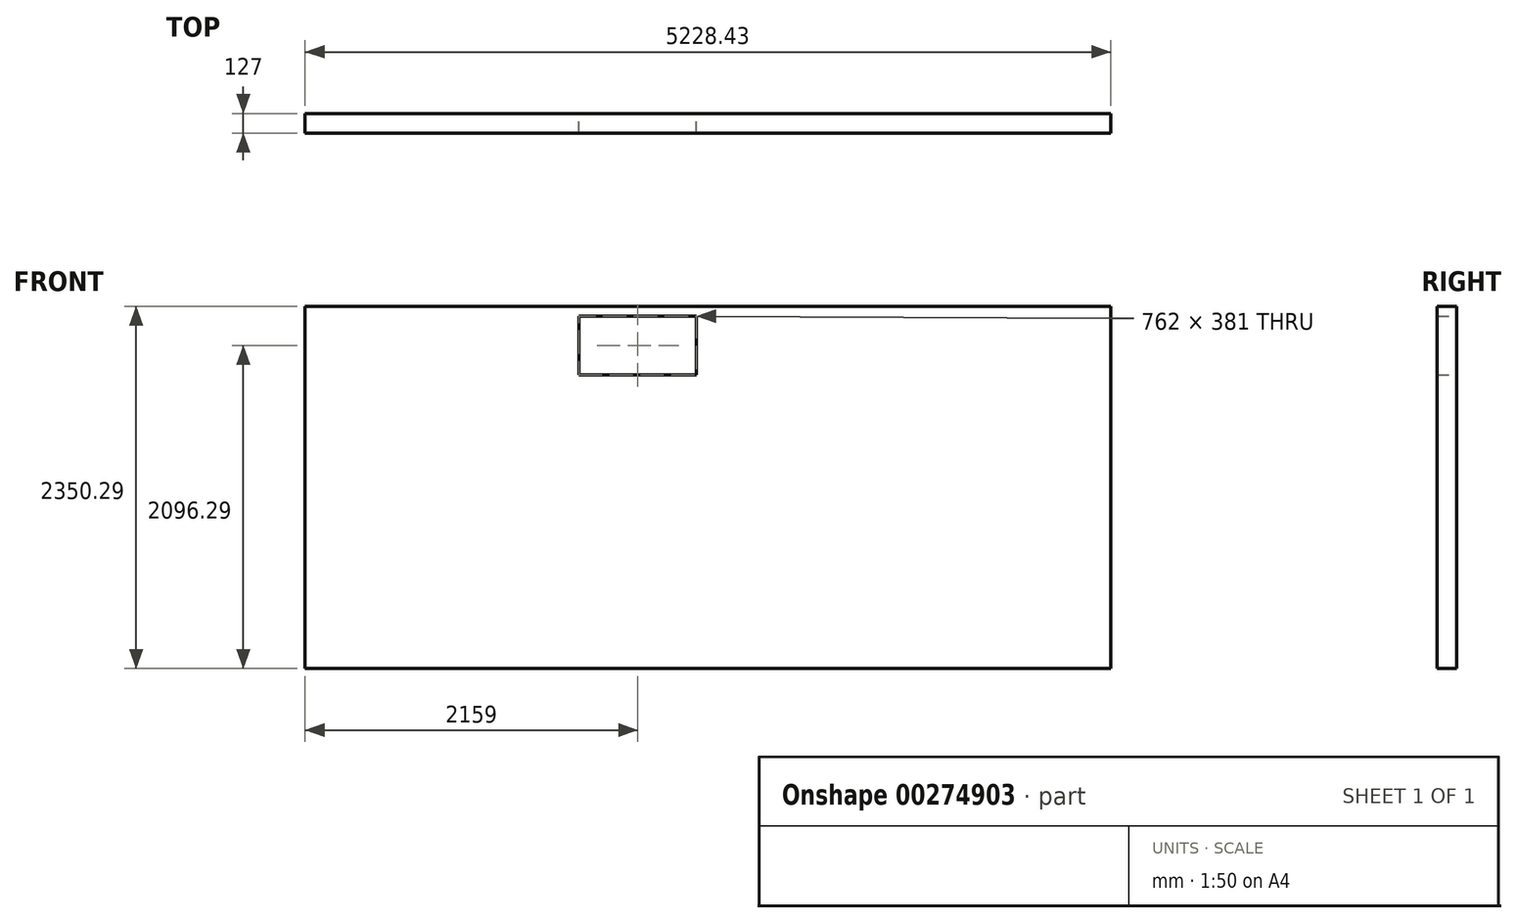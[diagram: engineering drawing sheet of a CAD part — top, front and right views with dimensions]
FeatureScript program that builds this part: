
annotation { "Feature Type Name" : "Feature", "Feature Type Description" : "" }
export const myFeature = defineFeature(function(context is Context, id is Id, definition is map)
    precondition{}
    {
        {
            var Q0;
            Q0=qCreatedBy(makeId("Top.planeOp"),FACE);
            var sketch = newSketch(context, id + "F0", { "sketchPlane" : qUnion([Q0])});
            skLineSegment(sketch, "E0.bottom", {"start": v(0, 0) * mm, "end": v(18288, 0) * mm});
            skLineSegment(sketch, "E0.top", {"start": v(0, 5486.4) * mm, "end": v(18288, 5486.4) * mm});
            skLineSegment(sketch, "E0.left", {"start": v(0, 0) * mm, "end": v(0, 5486.4) * mm});
            skLineSegment(sketch, "E0.right", {"start": v(18288, 0) * mm, "end": v(18288, 5486.4) * mm});
            skSolve(sketch);
        }
        {
            var Q0;
            Q0=makeQuery(id+"F0.imprint","IMPRINT",FACE,{"disambiguationData":[TD([[makeQuery(id+"F0.imprint","IMPRINT",EDGE,{"derivedFrom":sQuery(id+"F0.wireOp",EDGE,"E0.bottom")}),1.0]])]});
            extrude(context, id + "F1", {"entities" : qUnion([Q0]), "depth" : 101.6 * mm});
        }
        {
            var Q0;
            Q0=makeQuery(id+"F1.opExtrude","CAP_FACE",FACE,{"disambiguationData":[OSD([sQuery(id+"F0.wireOp",EDGE,"E0.bottom"),sQuery(id+"F0.wireOp",EDGE,"E0.top"),sQuery(id+"F0.wireOp",EDGE,"E0.left"),sQuery(id+"F0.wireOp",EDGE,"E0.right")])],"isStart":false});
            var sketch = newSketch(context, id + "F2", { "sketchPlane" : qUnion([Q0])});
            skLineSegment(sketch, "E1.bottom", {"start": v(18288, 5486.4) * mm, "end": v(13335, 5486.4) * mm, "construction": true});
            skLineSegment(sketch, "E1.top", {"start": v(18288, 2128.84) * mm, "end": v(13335, 2128.84) * mm, "construction": true});
            skLineSegment(sketch, "E1.left", {"start": v(18288, 5486.4) * mm, "end": v(18288, 2128.84) * mm, "construction": true});
            skLineSegment(sketch, "E1.right", {"start": v(13335, 5486.4) * mm, "end": v(13335, 2128.84) * mm, "construction": true});
            skLineSegment(sketch, "E2.bottom", {"start": v(18288, 2128.84) * mm, "end": v(13335, 2128.84) * mm});
            skLineSegment(sketch, "E2.top", {"start": v(18288, 1976.44) * mm, "end": v(13335, 1976.44) * mm});
            skLineSegment(sketch, "E2.left", {"start": v(18288, 2128.84) * mm, "end": v(18288, 1976.44) * mm});
            skLineSegment(sketch, "E2.right", {"start": v(13335, 2128.84) * mm, "end": v(13335, 1976.44) * mm});
            skLineSegment(sketch, "E3.bottom", {"start": v(13335, 5486.4) * mm, "end": v(13182.6, 5486.4) * mm});
            skLineSegment(sketch, "E3.top", {"start": v(13335, 2128.84) * mm, "end": v(13182.6, 2128.84) * mm});
            skLineSegment(sketch, "E3.left", {"start": v(13335, 5486.4) * mm, "end": v(13335, 2128.84) * mm});
            skLineSegment(sketch, "E3.right", {"start": v(13182.6, 5486.4) * mm, "end": v(13182.6, 2128.84) * mm});
            skLineSegment(sketch, "E4.bottom", {"start": v(13335, 1976.44) * mm, "end": v(13182.6, 1976.44) * mm});
            skLineSegment(sketch, "E4.left", {"start": v(13335, 1976.44) * mm, "end": v(13335, 2128.84) * mm});
            skLineSegment(sketch, "E4.right", {"start": v(13182.6, 1976.44) * mm, "end": v(13182.6, 2128.84) * mm});
            skSolve(sketch);
        }
        {
            var Q0;
            Q0=makeQuery(id+"F2.imprint","IMPRINT",FACE,{"disambiguationData":[TD([[makeQuery(id+"F2.imprint","IMPRINT",EDGE,{"derivedFrom":sQuery(id+"F2.wireOp",EDGE,"E2.bottom")}),1.0]])]});
            var Q1;
            Q1=makeQuery(id+"F2.imprint","IMPRINT",FACE,{"disambiguationData":[TD([[makeQuery(id+"F2.imprint","IMPRINT",EDGE,{"derivedFrom":sQuery(id+"F2.wireOp",EDGE,"E3.bottom")}),-1.0]])]});
            var Q2;
            Q2=makeQuery(id+"F2.imprint","IMPRINT",FACE,{"disambiguationData":[TD([[makeQuery(id+"F2.imprint","IMPRINT",EDGE,{"derivedFrom":sQuery(id+"F2.wireOp",EDGE,"E4.bottom")}),-1.0]])]});
            extrude(context, id + "F3", {"entities" : qUnion([Q0, Q1, Q2]), "operationType" : NewBodyOperationType.ADD, "depth" : 2426.5 * mm});
        }
        {
            var Q0;
            Q0=makeQuery(id+"F3.boolean.opBoolean","MERGE",FACE,{"derivedFrom":[makeQuery(id+"F1.opExtrude","SWEPT_FACE",FACE,{"disambiguationData":[OSD([sQuery(id+"F0.wireOp",EDGE,"E0.right")])]}),makeQuery(id+"F3.opExtrude","SWEPT_FACE",FACE,{"disambiguationData":[OSD([sQuery(id+"F2.wireOp",EDGE,"E2.left")])]})]});
            extrude(context, id + "F4", {"entities" : qUnion([Q0]), "operationType" : NewBodyOperationType.ADD, "depth" : 152.4 * mm});
        }
        {
            var Q0;
            {var subQ0=sQuery(id+"F0.wireOp",EDGE,"E0.top");Q0=makeQuery(id+"F4.boolean.opBoolean","MERGE",FACE,{"derivedFrom":[makeQuery(id+"F3.boolean.opBoolean","MERGE",FACE,{"derivedFrom":[makeQuery(id+"F1.opExtrude","SWEPT_FACE",FACE,{"disambiguationData":[OSD([subQ0])]}),makeQuery(id+"F3.opExtrude","SWEPT_FACE",FACE,{"disambiguationData":[OSD([sQuery(id+"F2.wireOp",EDGE,"E3.bottom")])]})]}),makeQuery(id+"F4.opExtrude","SWEPT_FACE",FACE,{"disambiguationData":[OSD([subQ0,sQuery(id+"F0.wireOp",EDGE,"E0.right")])]})]});}
            extrude(context, id + "F5", {"entities" : qUnion([Q0]), "operationType" : NewBodyOperationType.ADD, "depth" : 152.4 * mm});
        }
        {
            var Q0;
            {var subQ0=sQuery(id+"F0.wireOp",EDGE,"E0.right");var subQ1=sQuery(id+"F0.wireOp",EDGE,"E0.top");var subQ3=makeQuery(id+"F1.opExtrude","SWEPT_FACE",FACE,{"disambiguationData":[OSD([subQ0])]});var subQ4=makeQuery(id+"F1.opExtrude","SWEPT_FACE",FACE,{"disambiguationData":[OSD([subQ1])]});var subQ5=makeQuery(id+"F1.opExtrude","CAP_FACE",FACE,{"disambiguationData":[OSD([sQuery(id+"F0.wireOp",EDGE,"E0.bottom"),subQ1,sQuery(id+"F0.wireOp",EDGE,"E0.left"),subQ0])],"isStart":false});var subQ8=makeQuery(id+"F3.opExtrude","SWEPT_FACE",FACE,{"disambiguationData":[OSD([sQuery(id+"F2.wireOp",EDGE,"E2.bottom")])]});Q0=makeQuery(id+"F5.boolean.opBoolean","MERGE",FACE,{"derivedFrom":[makeQuery(id+"F4.boolean.opBoolean","MERGE",FACE,{"derivedFrom":[makeQuery(id+"F3.boolean.opBoolean","SPLIT",FACE,{"disambiguationData":[TD([subQ8])],"derivedFrom":subQ5}),makeQuery(id+"F4.opExtrude","SWEPT_FACE",FACE,{"disambiguationData":[OSD([subQ0]),TDD([makeQuery(id+"F3.boolean.opBoolean","SPLIT",EDGE,{"disambiguationData":[TD([subQ4])],"derivedFrom":makeQuery(id+"F1.opExtrude","CAP_EDGE",EDGE,{"disambiguationData":[OSD([subQ0])],"isStart":false})})])]})]}),makeQuery(id+"F5.opExtrude","SWEPT_FACE",FACE,{"disambiguationData":[OSD([subQ1,subQ0]),TDD([makeQuery(id+"F4.boolean.opBoolean","MERGE",EDGE,{"derivedFrom":[makeQuery(id+"F3.boolean.opBoolean","SPLIT",EDGE,{"disambiguationData":[TD([subQ3])],"derivedFrom":makeQuery(id+"F1.opExtrude","CAP_EDGE",EDGE,{"disambiguationData":[OSD([subQ1])],"isStart":false})}),makeQuery(id+"F4.opExtrude","SWEPT_EDGE",EDGE,{"disambiguationData":[OSD([subQ1,subQ0]),TDD([makeQuery(id+"F1.opExtrude","CAP_VERTEX",VERTEX,{"disambiguationData":[OSD([subQ1,subQ0])],"isStart":false})])]})]})])]})]});}
            var sketch = newSketch(context, id + "F6", { "sketchPlane" : qUnion([Q0])});
            skLineSegment(sketch, "E5.bottom", {"start": v(18440.4, 2128.84) * mm, "end": v(18288, 2128.84) * mm});
            skLineSegment(sketch, "E5.top", {"start": v(18440.4, 5638.8) * mm, "end": v(18288, 5638.8) * mm});
            skLineSegment(sketch, "E5.left", {"start": v(18440.4, 2128.84) * mm, "end": v(18440.4, 5638.8) * mm});
            skLineSegment(sketch, "E5.right", {"start": v(18288, 2128.84) * mm, "end": v(18288, 5638.8) * mm});
            skLineSegment(sketch, "E6.bottom", {"start": v(13335, 5638.8) * mm, "end": v(18288, 5638.8) * mm});
            skLineSegment(sketch, "E6.top", {"start": v(13335, 5486.4) * mm, "end": v(18288, 5486.4) * mm});
            skLineSegment(sketch, "E6.left", {"start": v(13335, 5638.8) * mm, "end": v(13335, 5486.4) * mm});
            skLineSegment(sketch, "E6.right", {"start": v(18288, 5638.8) * mm, "end": v(18288, 5486.4) * mm});
            skSolve(sketch);
        }
        {
            var Q0;
            Q0=makeQuery(id+"F6.imprint","IMPRINT",FACE,{"disambiguationData":[TD([[makeQuery(id+"F6.imprint","IMPRINT",EDGE,{"derivedFrom":sQuery(id+"F6.wireOp",EDGE,"E6.bottom")}),-1.0]])]});
            var Q1;
            Q1=makeQuery(id+"F6.imprint","IMPRINT",FACE,{"disambiguationData":[TD([[makeQuery(id+"F6.imprint","IMPRINT",EDGE,{"derivedFrom":sQuery(id+"F6.wireOp",EDGE,"E5.bottom")}),-1.0]])]});
            extrude(context, id + "F7", {"entities" : qUnion([Q0, Q1]), "operationType" : NewBodyOperationType.ADD, "depth" : 2350.3 * mm});
        }
        {
            var Q0;
            {var subQ0=sQuery(id+"F2.wireOp",EDGE,"E3.bottom");var subQ1=sQuery(id+"F2.wireOp",EDGE,"E2.left");Q0=makeQuery(id+"F5.boolean.opBoolean","MERGE",FACE,{"derivedFrom":[makeQuery(id+"F4.boolean.opBoolean","MERGE",FACE,{"derivedFrom":[makeQuery(id+"F3.opExtrude","CAP_FACE",FACE,{"disambiguationData":[OSD([sQuery(id+"F2.wireOp",EDGE,"E2.bottom"),sQuery(id+"F2.wireOp",EDGE,"E2.top"),subQ1,subQ0,sQuery(id+"F2.wireOp",EDGE,"E3.left"),sQuery(id+"F2.wireOp",EDGE,"E3.right"),sQuery(id+"F2.wireOp",EDGE,"E4.bottom"),sQuery(id+"F2.wireOp",EDGE,"E4.right")])],"isStart":false}),makeQuery(id+"F4.opExtrude","SWEPT_FACE",FACE,{"disambiguationData":[OSD([subQ1])]})]}),makeQuery(id+"F5.opExtrude","SWEPT_FACE",FACE,{"disambiguationData":[OSD([subQ0])]})]});}
            extrude(context, id + "F8", {"entities" : qUnion([Q0]), "operationType" : NewBodyOperationType.REMOVE, "oppositeDirection" : true, "depth" : 76.2 * mm});
        }
        {
            var Q0;
            {var subQ0=sQuery(id+"F0.wireOp",EDGE,"E0.right");var subQ1=sQuery(id+"F0.wireOp",EDGE,"E0.top");var subQ3=makeQuery(id+"F1.opExtrude","SWEPT_FACE",FACE,{"disambiguationData":[OSD([subQ0])]});var subQ4=makeQuery(id+"F1.opExtrude","SWEPT_FACE",FACE,{"disambiguationData":[OSD([subQ1])]});var subQ5=makeQuery(id+"F1.opExtrude","CAP_FACE",FACE,{"disambiguationData":[OSD([sQuery(id+"F0.wireOp",EDGE,"E0.bottom"),subQ1,sQuery(id+"F0.wireOp",EDGE,"E0.left"),subQ0])],"isStart":false});var subQ8=makeQuery(id+"F3.opExtrude","SWEPT_FACE",FACE,{"disambiguationData":[OSD([sQuery(id+"F2.wireOp",EDGE,"E2.bottom")])]});Q0=makeQuery(id+"F5.boolean.opBoolean","MERGE",FACE,{"derivedFrom":[makeQuery(id+"F4.boolean.opBoolean","MERGE",FACE,{"derivedFrom":[makeQuery(id+"F3.boolean.opBoolean","SPLIT",FACE,{"disambiguationData":[TD([subQ8])],"derivedFrom":subQ5}),makeQuery(id+"F4.opExtrude","SWEPT_FACE",FACE,{"disambiguationData":[OSD([subQ0]),TDD([makeQuery(id+"F3.boolean.opBoolean","SPLIT",EDGE,{"disambiguationData":[TD([subQ4])],"derivedFrom":makeQuery(id+"F1.opExtrude","CAP_EDGE",EDGE,{"disambiguationData":[OSD([subQ0])],"isStart":false})})])]})]}),makeQuery(id+"F5.opExtrude","SWEPT_FACE",FACE,{"disambiguationData":[OSD([subQ1,subQ0]),TDD([makeQuery(id+"F4.boolean.opBoolean","MERGE",EDGE,{"derivedFrom":[makeQuery(id+"F3.boolean.opBoolean","SPLIT",EDGE,{"disambiguationData":[TD([subQ3])],"derivedFrom":makeQuery(id+"F1.opExtrude","CAP_EDGE",EDGE,{"disambiguationData":[OSD([subQ1])],"isStart":false})}),makeQuery(id+"F4.opExtrude","SWEPT_EDGE",EDGE,{"disambiguationData":[OSD([subQ1,subQ0]),TDD([makeQuery(id+"F1.opExtrude","CAP_VERTEX",VERTEX,{"disambiguationData":[OSD([subQ1,subQ0])],"isStart":false})])]})]})])]})]});}
            var sketch = newSketch(context, id + "F9", { "sketchPlane" : qUnion([Q0])});
            skLineSegment(sketch, "E7.bottom", {"start": v(18288, 5486.4) * mm, "end": v(17907, 5486.4) * mm});
            skLineSegment(sketch, "E7.top", {"start": v(18288, 5207) * mm, "end": v(17907, 5207) * mm});
            skLineSegment(sketch, "E7.left", {"start": v(18288, 5486.4) * mm, "end": v(18288, 5207) * mm});
            skLineSegment(sketch, "E7.right", {"start": v(17907, 5486.4) * mm, "end": v(17907, 5207) * mm});
            skSolve(sketch);
        }
        {
            var Q0;
            Q0=makeQuery(id+"F9.imprint","IMPRINT",FACE,{"disambiguationData":[TD([[makeQuery(id+"F9.imprint","IMPRINT",EDGE,{"derivedFrom":sQuery(id+"F9.wireOp",EDGE,"E7.bottom")}),-1.0]])]});
            var Q1;
            Q1=makeQuery(id+"F8.boolean.opBoolean","MERGE",FACE,{"derivedFrom":[makeQuery(id+"F7.opExtrude","CAP_FACE",FACE,{"disambiguationData":[OSD([sQuery(id+"F6.wireOp",EDGE,"E5.bottom"),sQuery(id+"F6.wireOp",EDGE,"E5.top"),sQuery(id+"F6.wireOp",EDGE,"E5.left"),sQuery(id+"F6.wireOp",EDGE,"E5.right"),sQuery(id+"F6.wireOp",EDGE,"E6.bottom"),sQuery(id+"F6.wireOp",EDGE,"E6.top"),sQuery(id+"F6.wireOp",EDGE,"E6.left")])],"isStart":false}),makeQuery(id+"F8.opExtrude","CAP_FACE",FACE,{"disambiguationData":[OSD([sQuery(id+"F2.wireOp",EDGE,"E2.bottom"),sQuery(id+"F2.wireOp",EDGE,"E2.top"),sQuery(id+"F2.wireOp",EDGE,"E2.left"),sQuery(id+"F2.wireOp",EDGE,"E3.bottom"),sQuery(id+"F2.wireOp",EDGE,"E3.left"),sQuery(id+"F2.wireOp",EDGE,"E3.right"),sQuery(id+"F2.wireOp",EDGE,"E4.bottom"),sQuery(id+"F2.wireOp",EDGE,"E4.right")])],"isStart":false})]});
            extrude(context, id + "F10", {"entities" : qUnion([Q0]), "operationType" : NewBodyOperationType.ADD, "endBound" : BoundingType.UP_TO_SURFACE, "endBoundEntityFace" : qUnion([Q1]), "depth" : 25.4 * mm});
        }
        {
            var Q0;
            Q0=makeQuery(id+"F10.opExtrude","SWEPT_FACE",FACE,{"disambiguationData":[OSD([sQuery(id+"F9.wireOp",EDGE,"E7.top")])]});
            extrude(context, id + "F11", {"entities" : qUnion([Q0]), "operationType" : NewBodyOperationType.ADD, "depth" : 101.6 * mm});
        }
        {
            var Q0;
            {var subQ0=sQuery(id+"F9.wireOp",EDGE,"E7.right");Q0=makeQuery(id+"F11.boolean.opBoolean","MERGE",FACE,{"derivedFrom":[makeQuery(id+"F10.opExtrude","SWEPT_FACE",FACE,{"disambiguationData":[OSD([subQ0])]}),makeQuery(id+"F11.opExtrude","SWEPT_FACE",FACE,{"disambiguationData":[OSD([sQuery(id+"F9.wireOp",EDGE,"E7.top"),subQ0])]})]});}
            extrude(context, id + "F12", {"entities" : qUnion([Q0]), "operationType" : NewBodyOperationType.REMOVE, "oppositeDirection" : true, "depth" : 101.6 * mm});
        }
        {
            var Q0;
            {var subQ0=sQuery(id+"F2.wireOp",EDGE,"E3.right");Q0=makeQuery(id+"F5.boolean.opBoolean","MERGE",FACE,{"derivedFrom":[makeQuery(id+"F3.opExtrude","SWEPT_FACE",FACE,{"disambiguationData":[OSD([subQ0,sQuery(id+"F2.wireOp",EDGE,"E4.right")])]}),makeQuery(id+"F5.opExtrude","SWEPT_FACE",FACE,{"disambiguationData":[OSD([sQuery(id+"F0.wireOp",EDGE,"E0.top"),sQuery(id+"F2.wireOp",EDGE,"E3.bottom"),subQ0])]})]});}
            extrude(context, id + "F13", {"entities" : qUnion([Q0]), "operationType" : NewBodyOperationType.ADD, "depth" : 275.43 * mm});
        }
        {
            var Q0;
            {var subQ0=sQuery(id+"F2.wireOp",EDGE,"E3.left");Q0=makeQuery(id+"F5.boolean.opBoolean","MERGE",FACE,{"derivedFrom":[makeQuery(id+"F3.opExtrude","SWEPT_FACE",FACE,{"disambiguationData":[OSD([subQ0])]}),makeQuery(id+"F5.opExtrude","SWEPT_FACE",FACE,{"disambiguationData":[OSD([sQuery(id+"F0.wireOp",EDGE,"E0.top"),sQuery(id+"F2.wireOp",EDGE,"E3.bottom"),subQ0])]})]});}
            extrude(context, id + "F14", {"entities" : qUnion([Q0]), "operationType" : NewBodyOperationType.REMOVE, "oppositeDirection" : true, "depth" : 275.43 * mm});
        }
        {
            var Q0;
            {var subQ0=sQuery(id+"F2.wireOp",EDGE,"E4.bottom");var subQ1=sQuery(id+"F2.wireOp",EDGE,"E2.top");Q0=makeQuery(id+"F13.boolean.opBoolean","MERGE",FACE,{"derivedFrom":[makeQuery(id+"F4.boolean.opBoolean","MERGE",FACE,{"derivedFrom":[makeQuery(id+"F3.opExtrude","SWEPT_FACE",FACE,{"disambiguationData":[OSD([subQ1,subQ0])]}),makeQuery(id+"F4.opExtrude","SWEPT_FACE",FACE,{"disambiguationData":[OSD([sQuery(id+"F0.wireOp",EDGE,"E0.right"),subQ1,sQuery(id+"F2.wireOp",EDGE,"E2.left")])]})]}),makeQuery(id+"F13.opExtrude","SWEPT_FACE",FACE,{"disambiguationData":[OSD([subQ0,sQuery(id+"F2.wireOp",EDGE,"E4.right")])]})]});}
            extrude(context, id + "F15", {"entities" : qUnion([Q0]), "operationType" : NewBodyOperationType.REMOVE, "oppositeDirection" : true, "depth" : 25.4 * mm});
        }
        {
            var Q0;
            {var subQ0=sQuery(id+"F2.wireOp",EDGE,"E2.bottom");Q0=makeQuery(id+"F14.boolean.opBoolean","MERGE",FACE,{"derivedFrom":[makeQuery(id+"F4.boolean.opBoolean","MERGE",FACE,{"derivedFrom":[makeQuery(id+"F3.opExtrude","SWEPT_FACE",FACE,{"disambiguationData":[OSD([subQ0])]}),makeQuery(id+"F4.opExtrude","SWEPT_FACE",FACE,{"disambiguationData":[OSD([sQuery(id+"F0.wireOp",EDGE,"E0.right"),subQ0,sQuery(id+"F2.wireOp",EDGE,"E2.left")])]})]}),makeQuery(id+"F14.opExtrude","SWEPT_FACE",FACE,{"disambiguationData":[OSD([subQ0,sQuery(id+"F2.wireOp",EDGE,"E3.left"),sQuery(id+"F2.wireOp",EDGE,"E3.top"),sQuery(id+"F2.wireOp",EDGE,"E4.left")])]})]});}
            var sketch = newSketch(context, id + "F16", { "sketchPlane" : qUnion([Q0])});
            skLineSegment(sketch, "E8.bottom", {"start": v(-13059.57, 2451.9) * mm, "end": v(-14431.17, 2451.9) * mm, "construction": true});
            skLineSegment(sketch, "E8.top", {"start": v(-13059.57, 2197.9) * mm, "end": v(-14431.17, 2197.9) * mm, "construction": true});
            skLineSegment(sketch, "E8.left", {"start": v(-13059.57, 2451.9) * mm, "end": v(-13059.57, 2197.9) * mm, "construction": true});
            skLineSegment(sketch, "E8.right", {"start": v(-14431.17, 2451.9) * mm, "end": v(-14431.17, 2197.9) * mm, "construction": true});
            skLineSegment(sketch, "E9.bottom", {"start": v(-14431.17, 2197.9) * mm, "end": v(-15193.17, 2197.9) * mm});
            skLineSegment(sketch, "E9.top", {"start": v(-14431.17, 1943.9) * mm, "end": v(-15193.17, 1943.9) * mm});
            skLineSegment(sketch, "E9.left", {"start": v(-14431.17, 2197.9) * mm, "end": v(-14431.17, 1943.9) * mm});
            skLineSegment(sketch, "E9.right", {"start": v(-15193.17, 2197.9) * mm, "end": v(-15193.17, 1943.9) * mm});
            skSolve(sketch);
        }
        {
            var Q0;
            Q0=makeQuery(id+"F16.imprint","IMPRINT",FACE,{"disambiguationData":[TD([[makeQuery(id+"F16.imprint","IMPRINT",EDGE,{"derivedFrom":sQuery(id+"F16.wireOp",EDGE,"E9.bottom")}),1.0]])]});
            extrude(context, id + "F17", {"entities" : qUnion([Q0]), "operationType" : NewBodyOperationType.REMOVE, "endBound" : BoundingType.THROUGH_ALL, "oppositeDirection" : true, "depth" : 25.4 * mm});
        }
        {
            var Q0;
            Q0=makeQuery(id+"F17.boolean.opBoolean","COPY",FACE,{"derivedFrom":makeQuery(id+"F17.opExtrude","SWEPT_FACE",FACE,{"disambiguationData":[OSD([sQuery(id+"F16.wireOp",EDGE,"E9.bottom")])]})});
            extrude(context, id + "F18", {"entities" : qUnion([Q0]), "operationType" : NewBodyOperationType.REMOVE, "oppositeDirection" : true, "depth" : 190.5 * mm});
        }
        {
            var Q0;
            Q0=makeQuery(id+"F17.boolean.opBoolean","COPY",FACE,{"derivedFrom":makeQuery(id+"F17.opExtrude","SWEPT_FACE",FACE,{"disambiguationData":[OSD([sQuery(id+"F16.wireOp",EDGE,"E9.top")])]})});
            extrude(context, id + "F19", {"entities" : qUnion([Q0]), "operationType" : NewBodyOperationType.ADD, "depth" : 63.5 * mm});
        }
        {
            var Q0;
            Q0=makeQuery(id+"F7.opExtrude","SWEPT_FACE",FACE,{"disambiguationData":[OSD([sQuery(id+"F6.wireOp",EDGE,"E5.right")])]});
            var sketch = newSketch(context, id + "F20", { "sketchPlane" : qUnion([Q0])});
            skLineSegment(sketch, "E10.bottom", {"start": v(-5105.4, 2451.9) * mm, "end": v(-4851.4, 2451.9) * mm, "construction": true});
            skLineSegment(sketch, "E10.top", {"start": v(-5105.4, 2375.7) * mm, "end": v(-4851.4, 2375.7) * mm, "construction": true});
            skLineSegment(sketch, "E10.left", {"start": v(-5105.4, 2451.9) * mm, "end": v(-5105.4, 2375.7) * mm, "construction": true});
            skLineSegment(sketch, "E10.right", {"start": v(-4851.4, 2451.9) * mm, "end": v(-4851.4, 2375.7) * mm, "construction": true});
            skLineSegment(sketch, "E11.bottom", {"start": v(-4851.4, 2375.7) * mm, "end": v(-5105.4, 2375.7) * mm});
            skLineSegment(sketch, "E11.top", {"start": v(-4851.4, 2070.9) * mm, "end": v(-5105.4, 2070.9) * mm});
            skLineSegment(sketch, "E11.left", {"start": v(-4851.4, 2375.7) * mm, "end": v(-4851.4, 2070.9) * mm});
            skLineSegment(sketch, "E11.right", {"start": v(-5105.4, 2375.7) * mm, "end": v(-5105.4, 2070.9) * mm});
            skSolve(sketch);
        }
        {
            var Q0;
            Q0=makeQuery(id+"F20.imprint","IMPRINT",FACE,{"disambiguationData":[TD([[makeQuery(id+"F20.imprint","IMPRINT",EDGE,{"derivedFrom":sQuery(id+"F20.wireOp",EDGE,"E11.bottom")}),1.0]])]});
            extrude(context, id + "F21", {"entities" : qUnion([Q0]), "operationType" : NewBodyOperationType.REMOVE, "endBound" : BoundingType.THROUGH_ALL, "oppositeDirection" : true, "depth" : 25.4 * mm});
        }
        {
            var Q0;
            Q0=makeQuery(id+"F7.opExtrude","SWEPT_FACE",FACE,{"disambiguationData":[OSD([sQuery(id+"F6.wireOp",EDGE,"E5.right")])]});
            var sketch = newSketch(context, id + "F22", { "sketchPlane" : qUnion([Q0])});
            skLineSegment(sketch, "E12.bottom", {"start": v(-4851.4, 2375.7) * mm, "end": v(-3606.8, 2375.7) * mm, "construction": true});
            skLineSegment(sketch, "E12.top", {"start": v(-4851.4, 2070.9) * mm, "end": v(-3606.8, 2070.9) * mm, "construction": true});
            skLineSegment(sketch, "E12.left", {"start": v(-4851.4, 2375.7) * mm, "end": v(-4851.4, 2070.9) * mm, "construction": true});
            skLineSegment(sketch, "E12.right", {"start": v(-3606.8, 2375.7) * mm, "end": v(-3606.8, 2070.9) * mm, "construction": true});
            skLineSegment(sketch, "E13.bottom", {"start": v(-3606.8, 2375.7) * mm, "end": v(-3888.54, 2375.7) * mm});
            skLineSegment(sketch, "E13.top", {"start": v(-3606.8, 2070.9) * mm, "end": v(-3888.54, 2070.9) * mm});
            skLineSegment(sketch, "E13.left", {"start": v(-3606.8, 2375.7) * mm, "end": v(-3606.8, 2070.9) * mm});
            skLineSegment(sketch, "E13.right", {"start": v(-3888.54, 2375.7) * mm, "end": v(-3888.54, 2070.9) * mm});
            skSolve(sketch);
        }
        {
            var Q0;
            Q0=makeQuery(id+"F22.imprint","IMPRINT",FACE,{"disambiguationData":[TD([[makeQuery(id+"F22.imprint","IMPRINT",EDGE,{"derivedFrom":sQuery(id+"F22.wireOp",EDGE,"E13.bottom")}),1.0]])]});
            extrude(context, id + "F23", {"entities" : qUnion([Q0]), "operationType" : NewBodyOperationType.REMOVE, "endBound" : BoundingType.THROUGH_ALL, "oppositeDirection" : true, "depth" : 25.4 * mm});
        }
        {
            var Q0;
            Q0=makeQuery(id+"F23.boolean.opBoolean","COPY",FACE,{"derivedFrom":makeQuery(id+"F23.opExtrude","SWEPT_FACE",FACE,{"disambiguationData":[OSD([sQuery(id+"F22.wireOp",EDGE,"E13.right")])]})});
            extrude(context, id + "F24", {"entities" : qUnion([Q0]), "operationType" : NewBodyOperationType.REMOVE, "oppositeDirection" : true, "depth" : 304.8 * mm});
        }
        {
            var Q0;
            Q0=makeQuery(id+"F23.boolean.opBoolean","COPY",FACE,{"derivedFrom":makeQuery(id+"F23.opExtrude","SWEPT_FACE",FACE,{"disambiguationData":[OSD([sQuery(id+"F22.wireOp",EDGE,"E13.left")])]})});
            extrude(context, id + "F25", {"entities" : qUnion([Q0]), "operationType" : NewBodyOperationType.ADD, "depth" : 304.8 * mm});
        }
        {
            var Q0;
            Q0=makeQuery(id+"F24.boolean.opBoolean","COPY",FACE,{"derivedFrom":makeQuery(id+"F24.opExtrude","CAP_FACE",FACE,{"disambiguationData":[OSD([sQuery(id+"F22.wireOp",EDGE,"E13.right")])],"isStart":false})});
            extrude(context, id + "F26", {"entities" : qUnion([Q0]), "operationType" : NewBodyOperationType.ADD, "depth" : 25.4 * mm});
        }
        {
            var Q0;
            Q0=makeQuery(id+"F25.opExtrude","CAP_FACE",FACE,{"disambiguationData":[OSD([sQuery(id+"F22.wireOp",EDGE,"E13.left")])],"isStart":false});
            extrude(context, id + "F27", {"entities" : qUnion([Q0]), "operationType" : NewBodyOperationType.REMOVE, "oppositeDirection" : true, "depth" : 25.4 * mm});
        }
        {
            var Q0;
            Q0=makeQuery(id+"F27.boolean.opBoolean","COPY",FACE,{"derivedFrom":makeQuery(id+"F27.opExtrude","CAP_FACE",FACE,{"disambiguationData":[OSD([sQuery(id+"F22.wireOp",EDGE,"E13.left")])],"isStart":false})});
            extrude(context, id + "F28", {"entities" : qUnion([Q0]), "operationType" : NewBodyOperationType.REMOVE, "oppositeDirection" : true, "depth" : 12.7 * mm});
        }
        {
            var Q0;
            Q0=makeQuery(id+"F26.opExtrude","CAP_FACE",FACE,{"disambiguationData":[OSD([sQuery(id+"F22.wireOp",EDGE,"E13.right")])],"isStart":false});
            extrude(context, id + "F29", {"entities" : qUnion([Q0]), "operationType" : NewBodyOperationType.ADD, "depth" : 12.7 * mm});
        }
        {
            var Q0;
            Q0=makeQuery(id+"F13.opExtrude","CAP_FACE",FACE,{"disambiguationData":[OSD([sQuery(id+"F0.wireOp",EDGE,"E0.top"),sQuery(id+"F2.wireOp",EDGE,"E3.bottom"),sQuery(id+"F2.wireOp",EDGE,"E3.right"),sQuery(id+"F2.wireOp",EDGE,"E4.right")])],"isStart":false});
            var sketch = newSketch(context, id + "F30", { "sketchPlane" : qUnion([Q0])});
            skLineSegment(sketch, "E14.bottom", {"start": v(-2001.84, 2451.9) * mm, "end": v(-2408.24, 2451.9) * mm, "construction": true});
            skLineSegment(sketch, "E14.top", {"start": v(-2001.84, 1527.67) * mm, "end": v(-2408.24, 1527.67) * mm, "construction": true});
            skLineSegment(sketch, "E14.left", {"start": v(-2001.84, 2451.9) * mm, "end": v(-2001.84, 1527.67) * mm, "construction": true});
            skLineSegment(sketch, "E14.right", {"start": v(-2408.24, 2451.9) * mm, "end": v(-2408.24, 1527.67) * mm, "construction": true});
            skLineSegment(sketch, "E15.bottom", {"start": v(-2408.24, 2451.9) * mm, "end": v(-2535.24, 2451.9) * mm});
            skLineSegment(sketch, "E15.top", {"start": v(-2408.24, 101.6) * mm, "end": v(-2535.24, 101.6) * mm});
            skLineSegment(sketch, "E15.left", {"start": v(-2408.24, 2451.9) * mm, "end": v(-2408.24, 101.6) * mm});
            skLineSegment(sketch, "E15.right", {"start": v(-2535.24, 2451.9) * mm, "end": v(-2535.24, 101.6) * mm});
            skSolve(sketch);
        }
        {
            var Q0;
            Q0=makeQuery(id+"F30.imprint","IMPRINT",FACE,{"disambiguationData":[TD([[makeQuery(id+"F30.imprint","IMPRINT",EDGE,{"derivedFrom":sQuery(id+"F30.wireOp",EDGE,"E15.bottom")}),-1.0]])]});
            var Q1;
            {var subQ0=sQuery(id+"F0.wireOp",EDGE,"E0.left");Q1=makeQuery(id+"F5.boolean.opBoolean","MERGE",FACE,{"derivedFrom":[makeQuery(id+"F1.opExtrude","SWEPT_FACE",FACE,{"disambiguationData":[OSD([subQ0])]}),makeQuery(id+"F5.opExtrude","SWEPT_FACE",FACE,{"disambiguationData":[OSD([sQuery(id+"F0.wireOp",EDGE,"E0.top"),subQ0])]})]});}
            extrude(context, id + "F31", {"entities" : qUnion([Q0]), "operationType" : NewBodyOperationType.ADD, "endBound" : BoundingType.UP_TO_SURFACE, "endBoundEntityFace" : qUnion([Q1]), "depth" : 25.4 * mm});
        }
        {
            var Q0;
            Q0=makeQuery(id+"F31.opExtrude","SWEPT_FACE",FACE,{"disambiguationData":[OSD([sQuery(id+"F30.wireOp",EDGE,"E15.left")])]});
            var sketch = newSketch(context, id + "F32", { "sketchPlane" : qUnion([Q0])});
            skLineSegment(sketch, "E16.bottom", {"start": v(12907.17, 101.6) * mm, "end": v(12805.57, 101.6) * mm, "construction": true});
            skLineSegment(sketch, "E16.top", {"start": v(12907.17, 469.78) * mm, "end": v(12805.57, 469.78) * mm, "construction": true});
            skLineSegment(sketch, "E16.left", {"start": v(12907.17, 101.6) * mm, "end": v(12907.17, 469.78) * mm, "construction": true});
            skLineSegment(sketch, "E16.right", {"start": v(12805.57, 101.6) * mm, "end": v(12805.57, 469.78) * mm, "construction": true});
            skLineSegment(sketch, "E17.bottom", {"start": v(12805.57, 101.6) * mm, "end": v(11230.77, 101.6) * mm});
            skLineSegment(sketch, "E17.top", {"start": v(12805.57, 2235.2) * mm, "end": v(11230.77, 2235.2) * mm});
            skLineSegment(sketch, "E17.left", {"start": v(12805.57, 101.6) * mm, "end": v(12805.57, 2235.2) * mm});
            skLineSegment(sketch, "E17.right", {"start": v(11230.77, 101.6) * mm, "end": v(11230.77, 2235.2) * mm});
            skSolve(sketch);
        }
        {
            var Q0;
            Q0=makeQuery(id+"F32.imprint","IMPRINT",FACE,{"disambiguationData":[TD([[makeQuery(id+"F32.imprint","IMPRINT",EDGE,{"derivedFrom":sQuery(id+"F32.wireOp",EDGE,"E17.bottom")}),1.0]])]});
            extrude(context, id + "F33", {"entities" : qUnion([Q0]), "operationType" : NewBodyOperationType.REMOVE, "endBound" : BoundingType.THROUGH_ALL, "oppositeDirection" : true, "depth" : 25.4 * mm});
        }
        {
            var Q0;
            Q0=makeQuery(id+"F33.boolean.opBoolean","COPY",FACE,{"derivedFrom":makeQuery(id+"F33.opExtrude","SWEPT_FACE",FACE,{"disambiguationData":[OSD([sQuery(id+"F32.wireOp",EDGE,"E17.right")])]})});
            extrude(context, id + "F34", {"entities" : qUnion([Q0]), "operationType" : NewBodyOperationType.REMOVE, "oppositeDirection" : true, "depth" : 1320.8 * mm});
        }
        {
            var Q0;
            Q0=makeQuery(id+"F33.boolean.opBoolean","COPY",FACE,{"derivedFrom":makeQuery(id+"F33.opExtrude","SWEPT_FACE",FACE,{"disambiguationData":[OSD([sQuery(id+"F32.wireOp",EDGE,"E17.left")])]})});
            extrude(context, id + "F35", {"entities" : qUnion([Q0]), "operationType" : NewBodyOperationType.ADD, "depth" : 1320.8 * mm});
        }
        {
            var Q0;
            {var subQ0=sQuery(id+"F22.wireOp",EDGE,"E13.left");var subQ1=sQuery(id+"F22.wireOp",EDGE,"E13.top");Q0=makeQuery(id+"F28.boolean.opBoolean","MERGE",FACE,{"derivedFrom":[makeQuery(id+"F27.boolean.opBoolean","MERGE",FACE,{"derivedFrom":[makeQuery(id+"F24.boolean.opBoolean","MERGE",FACE,{"derivedFrom":[makeQuery(id+"F23.boolean.opBoolean","COPY",FACE,{"derivedFrom":makeQuery(id+"F23.opExtrude","SWEPT_FACE",FACE,{"disambiguationData":[OSD([subQ1])]})}),makeQuery(id+"F24.opExtrude","SWEPT_FACE",FACE,{"disambiguationData":[OSD([subQ1,sQuery(id+"F22.wireOp",EDGE,"E13.right")])]})]}),makeQuery(id+"F27.opExtrude","SWEPT_FACE",FACE,{"disambiguationData":[OSD([subQ1,subQ0])]})]}),makeQuery(id+"F28.opExtrude","SWEPT_FACE",FACE,{"disambiguationData":[OSD([subQ1,subQ0])]})]});}
            extrude(context, id + "F36", {"entities" : qUnion([Q0]), "operationType" : NewBodyOperationType.ADD, "depth" : 120.65 * mm});
        }
        {
            var Q0;
            {var subQ0=sQuery(id+"F22.wireOp",EDGE,"E13.left");var subQ1=sQuery(id+"F22.wireOp",EDGE,"E13.bottom");Q0=makeQuery(id+"F28.boolean.opBoolean","MERGE",FACE,{"derivedFrom":[makeQuery(id+"F27.boolean.opBoolean","MERGE",FACE,{"derivedFrom":[makeQuery(id+"F24.boolean.opBoolean","MERGE",FACE,{"derivedFrom":[makeQuery(id+"F23.boolean.opBoolean","COPY",FACE,{"derivedFrom":makeQuery(id+"F23.opExtrude","SWEPT_FACE",FACE,{"disambiguationData":[OSD([subQ1])]})}),makeQuery(id+"F24.opExtrude","SWEPT_FACE",FACE,{"disambiguationData":[OSD([subQ1,sQuery(id+"F22.wireOp",EDGE,"E13.right")])]})]}),makeQuery(id+"F27.opExtrude","SWEPT_FACE",FACE,{"disambiguationData":[OSD([subQ1,subQ0])]})]}),makeQuery(id+"F28.opExtrude","SWEPT_FACE",FACE,{"disambiguationData":[OSD([subQ1,subQ0])]})]});}
            extrude(context, id + "F37", {"entities" : qUnion([Q0]), "operationType" : NewBodyOperationType.REMOVE, "endBound" : BoundingType.THROUGH_ALL, "oppositeDirection" : true, "depth" : 25.4 * mm});
        }
        {
            var Q0;
            Q0=makeQuery(id+"F21.boolean.opBoolean","COPY",FACE,{"derivedFrom":makeQuery(id+"F21.opExtrude","SWEPT_FACE",FACE,{"disambiguationData":[OSD([sQuery(id+"F20.wireOp",EDGE,"E11.top")])]})});
            extrude(context, id + "F38", {"entities" : qUnion([Q0]), "operationType" : NewBodyOperationType.REMOVE, "oppositeDirection" : true, "depth" : 190.5 * mm});
        }
        {
            var Q0;
            Q0=makeQuery(id+"F21.boolean.opBoolean","COPY",FACE,{"derivedFrom":makeQuery(id+"F21.opExtrude","SWEPT_FACE",FACE,{"disambiguationData":[OSD([sQuery(id+"F20.wireOp",EDGE,"E11.bottom")])]})});
            extrude(context, id + "F39", {"entities" : qUnion([Q0]), "operationType" : NewBodyOperationType.ADD, "depth" : 190.5 * mm});
        }
        {
            var Q0;
            Q0=makeQuery(id+"F39.opExtrude","CAP_FACE",FACE,{"disambiguationData":[OSD([sQuery(id+"F20.wireOp",EDGE,"E11.bottom")])],"isStart":false});
            extrude(context, id + "F40", {"entities" : qUnion([Q0]), "operationType" : NewBodyOperationType.REMOVE, "oppositeDirection" : true, "depth" : 76.2 * mm});
        }
        {
            var Q0;
            {var subQ0=sQuery(id+"F16.wireOp",EDGE,"E9.right");Q0=makeQuery(id+"F18.boolean.opBoolean","MERGE",FACE,{"derivedFrom":[makeQuery(id+"F17.boolean.opBoolean","COPY",FACE,{"derivedFrom":makeQuery(id+"F17.opExtrude","SWEPT_FACE",FACE,{"disambiguationData":[OSD([subQ0])]})}),makeQuery(id+"F18.opExtrude","SWEPT_FACE",FACE,{"disambiguationData":[OSD([sQuery(id+"F16.wireOp",EDGE,"E9.bottom"),subQ0])]})]});}
            extrude(context, id + "F41", {"entities" : qUnion([Q0]), "operationType" : NewBodyOperationType.REMOVE, "oppositeDirection" : true, "depth" : 406.4 * mm});
        }
        {
            var Q0;
            {var subQ0=sQuery(id+"F16.wireOp",EDGE,"E9.left");Q0=makeQuery(id+"F18.boolean.opBoolean","MERGE",FACE,{"derivedFrom":[makeQuery(id+"F17.boolean.opBoolean","COPY",FACE,{"derivedFrom":makeQuery(id+"F17.opExtrude","SWEPT_FACE",FACE,{"disambiguationData":[OSD([subQ0])]})}),makeQuery(id+"F18.opExtrude","SWEPT_FACE",FACE,{"disambiguationData":[OSD([sQuery(id+"F16.wireOp",EDGE,"E9.bottom"),subQ0])]})]});}
            extrude(context, id + "F42", {"entities" : qUnion([Q0]), "operationType" : NewBodyOperationType.ADD, "depth" : 406.4 * mm});
        }
        {
            var Q0;
            {var subQ0=sQuery(id+"F22.wireOp",EDGE,"E13.left");Q0=makeQuery(id+"F37.boolean.opBoolean","MERGE",FACE,{"derivedFrom":[makeQuery(id+"F28.boolean.opBoolean","COPY",FACE,{"derivedFrom":makeQuery(id+"F28.opExtrude","CAP_FACE",FACE,{"disambiguationData":[OSD([subQ0])],"isStart":false})}),makeQuery(id+"F37.opExtrude","SWEPT_FACE",FACE,{"disambiguationData":[OSD([sQuery(id+"F22.wireOp",EDGE,"E13.bottom"),subQ0])]})]});}
            extrude(context, id + "F43", {"entities" : qUnion([Q0]), "operationType" : NewBodyOperationType.REMOVE, "oppositeDirection" : true, "depth" : 76.2 * mm});
        }
        {
            var Q0;
            {var subQ0=sQuery(id+"F22.wireOp",EDGE,"E13.right");Q0=makeQuery(id+"F37.boolean.opBoolean","MERGE",FACE,{"derivedFrom":[makeQuery(id+"F29.opExtrude","CAP_FACE",FACE,{"disambiguationData":[OSD([subQ0])],"isStart":false}),makeQuery(id+"F37.opExtrude","SWEPT_FACE",FACE,{"disambiguationData":[OSD([sQuery(id+"F22.wireOp",EDGE,"E13.bottom"),subQ0])]})]});}
            extrude(context, id + "F44", {"entities" : qUnion([Q0]), "operationType" : NewBodyOperationType.REMOVE, "oppositeDirection" : true, "depth" : 60.96 * mm});
        }
        {
            var Q0;
            Q0=makeQuery(id+"F38.boolean.opBoolean","COPY",FACE,{"derivedFrom":makeQuery(id+"F38.opExtrude","CAP_FACE",FACE,{"disambiguationData":[OSD([sQuery(id+"F20.wireOp",EDGE,"E11.top")])],"isStart":false})});
            extrude(context, id + "F45", {"entities" : qUnion([Q0]), "operationType" : NewBodyOperationType.ADD, "depth" : 25.4 * mm});
        }
        {
            var Q0;
            Q0=makeQuery(id+"F40.boolean.opBoolean","COPY",FACE,{"derivedFrom":makeQuery(id+"F40.opExtrude","CAP_FACE",FACE,{"disambiguationData":[OSD([sQuery(id+"F20.wireOp",EDGE,"E11.bottom")])],"isStart":false})});
            extrude(context, id + "F46", {"entities" : qUnion([Q0]), "operationType" : NewBodyOperationType.REMOVE, "oppositeDirection" : true, "depth" : 63.5 * mm});
        }
        {
            var Q0;
            {var subQ0=sQuery(id+"F0.wireOp",EDGE,"E0.right");var subQ1=sQuery(id+"F0.wireOp",EDGE,"E0.top");Q0=makeQuery(id+"F5.boolean.opBoolean","MERGE",FACE,{"derivedFrom":[makeQuery(id+"F4.boolean.opBoolean","MERGE",FACE,{"derivedFrom":[makeQuery(id+"F1.opExtrude","CAP_FACE",FACE,{"disambiguationData":[OSD([sQuery(id+"F0.wireOp",EDGE,"E0.bottom"),subQ1,sQuery(id+"F0.wireOp",EDGE,"E0.left"),subQ0])],"isStart":true}),makeQuery(id+"F4.opExtrude","SWEPT_FACE",FACE,{"disambiguationData":[OSD([subQ0]),TDD([makeQuery(id+"F1.opExtrude","CAP_EDGE",EDGE,{"disambiguationData":[OSD([subQ0])],"isStart":true})])]})]}),makeQuery(id+"F5.opExtrude","SWEPT_FACE",FACE,{"disambiguationData":[OSD([subQ1,subQ0]),TDD([makeQuery(id+"F4.boolean.opBoolean","MERGE",EDGE,{"derivedFrom":[makeQuery(id+"F1.opExtrude","CAP_EDGE",EDGE,{"disambiguationData":[OSD([subQ1])],"isStart":true}),makeQuery(id+"F4.opExtrude","SWEPT_EDGE",EDGE,{"disambiguationData":[OSD([subQ1,subQ0]),TDD([makeQuery(id+"F1.opExtrude","CAP_VERTEX",VERTEX,{"disambiguationData":[OSD([subQ1,subQ0])],"isStart":true})])]})]})])]})]});}
            var Q1;
            {var subQ0=sQuery(id+"F32.wireOp",EDGE,"E17.bottom");var subQ1=sQuery(id+"F30.wireOp",EDGE,"E15.left");var subQ2=sQuery(id+"F2.wireOp",EDGE,"E4.right");var subQ3=sQuery(id+"F2.wireOp",EDGE,"E3.right");var subQ4=sQuery(id+"F2.wireOp",EDGE,"E3.bottom");var subQ5=sQuery(id+"F0.wireOp",EDGE,"E0.top");var subQ6=sQuery(id+"F0.wireOp",EDGE,"E0.right");var subQ7=sQuery(id+"F0.wireOp",EDGE,"E0.left");var subQ12=sQuery(id+"F2.wireOp",EDGE,"E4.bottom");var subQ13=sQuery(id+"F2.wireOp",EDGE,"E2.left");var subQ14=sQuery(id+"F2.wireOp",EDGE,"E2.top");var subQ16=sQuery(id+"F0.wireOp",EDGE,"E0.bottom");var subQ17=makeQuery(id+"F1.opExtrude","CAP_FACE",FACE,{"disambiguationData":[OSD([subQ16,subQ5,subQ7,subQ6])],"isStart":false});var subQ20=makeQuery(id+"F1.opExtrude","SWEPT_FACE",FACE,{"disambiguationData":[OSD([subQ16])]});var subQ21=makeQuery(id+"F15.boolean.opBoolean","MERGE",FACE,{"derivedFrom":[makeQuery(id+"F5.boolean.opBoolean","MERGE",FACE,{"derivedFrom":[makeQuery(id+"F4.boolean.opBoolean","MERGE",FACE,{"derivedFrom":[makeQuery(id+"F3.boolean.opBoolean","SPLIT",FACE,{"disambiguationData":[TD([subQ20])],"derivedFrom":subQ17}),makeQuery(id+"F4.opExtrude","SWEPT_FACE",FACE,{"disambiguationData":[OSD([subQ6]),TDD([makeQuery(id+"F3.boolean.opBoolean","SPLIT",EDGE,{"disambiguationData":[TD([subQ20])],"derivedFrom":makeQuery(id+"F1.opExtrude","CAP_EDGE",EDGE,{"disambiguationData":[OSD([subQ6])],"isStart":false})})])]})]}),makeQuery(id+"F5.opExtrude","SWEPT_FACE",FACE,{"disambiguationData":[OSD([subQ5])]})]}),makeQuery(id+"F15.opExtrude","SWEPT_FACE",FACE,{"disambiguationData":[OSD([subQ6,subQ14,subQ13,subQ12,subQ2]),TDD([makeQuery(id+"F13.boolean.opBoolean","MERGE",EDGE,{"derivedFrom":[makeQuery(id+"F4.boolean.opBoolean","MERGE",EDGE,{"derivedFrom":[makeQuery(id+"F3.opExtrude","CAP_EDGE",EDGE,{"disambiguationData":[OSD([subQ14,subQ12])],"isStart":true}),makeQuery(id+"F4.opExtrude","SWEPT_EDGE",EDGE,{"disambiguationData":[OSD([subQ6,subQ14,subQ13]),TDD([makeQuery(id+"F3.opExtrude","CAP_VERTEX",VERTEX,{"disambiguationData":[OSD([subQ6,subQ14,subQ13])],"isStart":true})])]})]}),makeQuery(id+"F13.opExtrude","SWEPT_EDGE",EDGE,{"disambiguationData":[OSD([subQ12,subQ2]),TDD([makeQuery(id+"F3.opExtrude","CAP_VERTEX",VERTEX,{"disambiguationData":[OSD([subQ12,subQ2])],"isStart":true})])]})]})])]})]});Q1=makeQuery(id+"F34.boolean.opBoolean","MERGE",FACE,{"derivedFrom":[makeQuery(id+"F33.boolean.opBoolean","MERGE",FACE,{"derivedFrom":[makeQuery(id+"F31.boolean.opBoolean","SPLIT",FACE,{"disambiguationData":[TD([subQ20])],"derivedFrom":subQ21}),makeQuery(id+"F31.boolean.opBoolean","SPLIT",FACE,{"disambiguationData":[TD([makeQuery(id+"F31.opExtrude","SWEPT_FACE",FACE,{"disambiguationData":[OSD([sQuery(id+"F30.wireOp",EDGE,"E15.right")])]})])],"derivedFrom":subQ21}),makeQuery(id+"F33.opExtrude","SWEPT_FACE",FACE,{"disambiguationData":[OSD([subQ0])]})]}),makeQuery(id+"F34.opExtrude","SWEPT_FACE",FACE,{"disambiguationData":[OSD([subQ5,subQ4,subQ3,subQ2,sQuery(id+"F30.wireOp",EDGE,"E15.top"),subQ1,subQ0,sQuery(id+"F32.wireOp",EDGE,"E17.right")])]})]});}
            extrude(context, id + "F47", {"entities" : qUnion([Q0]), "operationType" : NewBodyOperationType.REMOVE, "endBound" : BoundingType.UP_TO_SURFACE, "oppositeDirection" : true, "endBoundEntityFace" : qUnion([Q1]), "depth" : 25.4 * mm});
        }
        {
            var Q0;
            {var subQ0=sQuery(id+"F0.wireOp",EDGE,"E0.left");var subQ1=sQuery(id+"F0.wireOp",EDGE,"E0.top");Q0=makeQuery(id+"F31.boolean.opBoolean","MERGE",FACE,{"derivedFrom":[makeQuery(id+"F5.boolean.opBoolean","MERGE",FACE,{"derivedFrom":[makeQuery(id+"F1.opExtrude","SWEPT_FACE",FACE,{"disambiguationData":[OSD([subQ0])]}),makeQuery(id+"F5.opExtrude","SWEPT_FACE",FACE,{"disambiguationData":[OSD([subQ1,subQ0])]})]}),makeQuery(id+"F31.opExtrude","CAP_FACE",FACE,{"disambiguationData":[OSD([subQ1,subQ0])],"isStart":false})]});}
            var Q1;
            {var subQ0=sQuery(id+"F2.wireOp",EDGE,"E4.right");var subQ1=sQuery(id+"F2.wireOp",EDGE,"E3.right");var subQ2=sQuery(id+"F2.wireOp",EDGE,"E3.bottom");var subQ3=sQuery(id+"F0.wireOp",EDGE,"E0.top");Q1=makeQuery(id+"F31.boolean.opBoolean","SPLIT",FACE,{"disambiguationData":[TD([makeQuery(id+"F31.opExtrude","SWEPT_FACE",FACE,{"disambiguationData":[OSD([sQuery(id+"F30.wireOp",EDGE,"E15.right")])]})])],"derivedFrom":makeQuery(id+"F13.opExtrude","CAP_FACE",FACE,{"disambiguationData":[OSD([subQ3,subQ2,subQ1,subQ0])],"isStart":false})});}
            extrude(context, id + "F48", {"entities" : qUnion([Q0]), "operationType" : NewBodyOperationType.REMOVE, "endBound" : BoundingType.UP_TO_SURFACE, "oppositeDirection" : true, "endBoundEntityFace" : qUnion([Q1]), "depth" : 25.4 * mm});
        }
        {
            var Q0;
            {var subQ0=sQuery(id+"F0.wireOp",EDGE,"E0.left");var subQ1=sQuery(id+"F0.wireOp",EDGE,"E0.top");var subQ2=sQuery(id+"F2.wireOp",EDGE,"E4.right");var subQ15=sQuery(id+"F2.wireOp",EDGE,"E3.right");var subQ17=sQuery(id+"F2.wireOp",EDGE,"E3.bottom");var subQ29=makeQuery(id+"F13.opExtrude","CAP_FACE",FACE,{"disambiguationData":[OSD([subQ1,subQ17,subQ15,subQ2])],"isStart":false});Q0=makeQuery(id+"F48.boolean.opBoolean","MERGE",FACE,{"derivedFrom":[makeQuery(id+"F31.boolean.opBoolean","SPLIT",FACE,{"disambiguationData":[TD([makeQuery(id+"F31.opExtrude","SWEPT_FACE",FACE,{"disambiguationData":[OSD([sQuery(id+"F30.wireOp",EDGE,"E15.right")])]})])],"derivedFrom":subQ29}),makeQuery(id+"F31.boolean.opBoolean","SPLIT",FACE,{"disambiguationData":[TD([makeQuery(id+"F31.opExtrude","SWEPT_FACE",FACE,{"disambiguationData":[OSD([sQuery(id+"F30.wireOp",EDGE,"E15.left")])]})])],"derivedFrom":subQ29})],"fromTools":[makeQuery(id+"F48.opExtrude","CAP_FACE",FACE,{"disambiguationData":[OSD([subQ1,subQ0])],"isStart":false})]});}
            var Q1;
            Q1=makeQuery(id+"F14.boolean.opBoolean","COPY",FACE,{"derivedFrom":makeQuery(id+"F14.opExtrude","CAP_FACE",FACE,{"disambiguationData":[OSD([sQuery(id+"F0.wireOp",EDGE,"E0.top"),sQuery(id+"F2.wireOp",EDGE,"E3.bottom"),sQuery(id+"F2.wireOp",EDGE,"E3.left")])],"isStart":false})});
            extrude(context, id + "F49", {"entities" : qUnion([Q0]), "operationType" : NewBodyOperationType.REMOVE, "endBound" : BoundingType.UP_TO_SURFACE, "oppositeDirection" : true, "endBoundEntityFace" : qUnion([Q1]), "depth" : 25.4 * mm});
        }
        {
            var Q0;
            {var subQ0=sQuery(id+"F6.wireOp",EDGE,"E5.left");var subQ1=sQuery(id+"F2.wireOp",EDGE,"E2.left");var subQ2=sQuery(id+"F0.wireOp",EDGE,"E0.right");var subQ3=sQuery(id+"F0.wireOp",EDGE,"E0.top");var subQ4=sQuery(id+"F22.wireOp",EDGE,"E13.right");var subQ5=sQuery(id+"F22.wireOp",EDGE,"E13.left");Q0=makeQuery(id+"F45.boolean.opBoolean","MERGE",FACE,{"derivedFrom":[makeQuery(id+"F39.boolean.opBoolean","MERGE",FACE,{"derivedFrom":[makeQuery(id+"F36.boolean.opBoolean","MERGE",FACE,{"derivedFrom":[makeQuery(id+"F29.boolean.opBoolean","MERGE",FACE,{"derivedFrom":[makeQuery(id+"F26.boolean.opBoolean","MERGE",FACE,{"derivedFrom":[makeQuery(id+"F25.boolean.opBoolean","MERGE",FACE,{"derivedFrom":[makeQuery(id+"F7.boolean.opBoolean","MERGE",FACE,{"derivedFrom":[makeQuery(id+"F5.boolean.opBoolean","MERGE",FACE,{"derivedFrom":[makeQuery(id+"F4.opExtrude","CAP_FACE",FACE,{"disambiguationData":[OSD([subQ2,subQ1])],"isStart":false}),makeQuery(id+"F5.opExtrude","SWEPT_FACE",FACE,{"disambiguationData":[OSD([subQ3,subQ2]),TDD([makeQuery(id+"F4.opExtrude","CAP_EDGE",EDGE,{"disambiguationData":[OSD([subQ3,subQ2])],"isStart":false})])]})]}),makeQuery(id+"F7.opExtrude","SWEPT_FACE",FACE,{"disambiguationData":[OSD([subQ0])]})]}),makeQuery(id+"F25.opExtrude","SWEPT_FACE",FACE,{"disambiguationData":[OSD([subQ3,subQ2,subQ1,subQ0,subQ5])]})]}),makeQuery(id+"F26.opExtrude","SWEPT_FACE",FACE,{"disambiguationData":[OSD([subQ3,subQ2,subQ1,subQ0,subQ4])]})]}),makeQuery(id+"F29.opExtrude","SWEPT_FACE",FACE,{"disambiguationData":[OSD([subQ3,subQ2,subQ1,subQ0,subQ4])]})]}),makeQuery(id+"F36.opExtrude","SWEPT_FACE",FACE,{"disambiguationData":[OSD([subQ3,subQ2,subQ1,subQ0,sQuery(id+"F22.wireOp",EDGE,"E13.top"),subQ5,subQ4])]})]}),makeQuery(id+"F39.opExtrude","SWEPT_FACE",FACE,{"disambiguationData":[OSD([subQ3,subQ2,subQ1,subQ0,sQuery(id+"F20.wireOp",EDGE,"E11.bottom")])]})]}),makeQuery(id+"F45.opExtrude","SWEPT_FACE",FACE,{"disambiguationData":[OSD([subQ3,subQ2,subQ1,subQ0,sQuery(id+"F20.wireOp",EDGE,"E11.top")])]})]});}
            var Q1;
            {var subQ0=sQuery(id+"F22.wireOp",EDGE,"E13.right");var subQ1=sQuery(id+"F22.wireOp",EDGE,"E13.left");Q1=makeQuery(id+"F45.boolean.opBoolean","MERGE",FACE,{"derivedFrom":[makeQuery(id+"F39.boolean.opBoolean","MERGE",FACE,{"derivedFrom":[makeQuery(id+"F36.boolean.opBoolean","MERGE",FACE,{"derivedFrom":[makeQuery(id+"F29.boolean.opBoolean","MERGE",FACE,{"derivedFrom":[makeQuery(id+"F26.boolean.opBoolean","MERGE",FACE,{"derivedFrom":[makeQuery(id+"F25.boolean.opBoolean","MERGE",FACE,{"derivedFrom":[makeQuery(id+"F7.opExtrude","SWEPT_FACE",FACE,{"disambiguationData":[OSD([sQuery(id+"F6.wireOp",EDGE,"E5.right")])]}),makeQuery(id+"F25.opExtrude","SWEPT_FACE",FACE,{"disambiguationData":[OSD([subQ1])]})]}),makeQuery(id+"F26.opExtrude","SWEPT_FACE",FACE,{"disambiguationData":[OSD([subQ0])]})]}),makeQuery(id+"F29.opExtrude","SWEPT_FACE",FACE,{"disambiguationData":[OSD([subQ0])]})]}),makeQuery(id+"F36.opExtrude","SWEPT_FACE",FACE,{"disambiguationData":[OSD([sQuery(id+"F22.wireOp",EDGE,"E13.top"),subQ1,subQ0])]})]}),makeQuery(id+"F39.opExtrude","SWEPT_FACE",FACE,{"disambiguationData":[OSD([sQuery(id+"F20.wireOp",EDGE,"E11.bottom")])]})]}),makeQuery(id+"F45.opExtrude","SWEPT_FACE",FACE,{"disambiguationData":[OSD([sQuery(id+"F20.wireOp",EDGE,"E11.top")])]})]});}
            extrude(context, id + "F50", {"entities" : qUnion([Q0]), "operationType" : NewBodyOperationType.REMOVE, "endBound" : BoundingType.UP_TO_SURFACE, "oppositeDirection" : true, "endBoundEntityFace" : qUnion([Q1]), "depth" : 25.4 * mm});
        }
        {
            var Q0;
            {var subQ0=sQuery(id+"F2.wireOp",EDGE,"E3.bottom");var subQ1=sQuery(id+"F0.wireOp",EDGE,"E0.top");Q0=makeQuery(id+"F13.boolean.opBoolean","MERGE",FACE,{"derivedFrom":[makeQuery(id+"F7.boolean.opBoolean","MERGE",FACE,{"derivedFrom":[makeQuery(id+"F5.opExtrude","CAP_FACE",FACE,{"disambiguationData":[OSD([subQ1,sQuery(id+"F0.wireOp",EDGE,"E0.right"),subQ0])],"isStart":false}),makeQuery(id+"F7.opExtrude","SWEPT_FACE",FACE,{"disambiguationData":[OSD([sQuery(id+"F6.wireOp",EDGE,"E5.top"),sQuery(id+"F6.wireOp",EDGE,"E6.bottom")])]})]}),makeQuery(id+"F13.opExtrude","SWEPT_FACE",FACE,{"disambiguationData":[OSD([subQ1,subQ0,sQuery(id+"F2.wireOp",EDGE,"E3.right")])]})]});}
            var Q1;
            {var subQ0=sQuery(id+"F20.wireOp",EDGE,"E11.right");var subQ1=sQuery(id+"F20.wireOp",EDGE,"E11.bottom");var subQ2=sQuery(id+"F9.wireOp",EDGE,"E7.left");var subQ3=sQuery(id+"F9.wireOp",EDGE,"E7.top");var subQ4=sQuery(id+"F6.wireOp",EDGE,"E5.right");Q1=makeQuery(id+"F46.boolean.opBoolean","MERGE",FACE,{"derivedFrom":[makeQuery(id+"F40.boolean.opBoolean","MERGE",FACE,{"derivedFrom":[makeQuery(id+"F38.boolean.opBoolean","MERGE",FACE,{"derivedFrom":[makeQuery(id+"F21.boolean.opBoolean","MERGE",FACE,{"derivedFrom":[makeQuery(id+"F11.opExtrude","CAP_FACE",FACE,{"disambiguationData":[OSD([subQ3])],"isStart":false}),makeQuery(id+"F21.opExtrude","SWEPT_FACE",FACE,{"disambiguationData":[OSD([subQ0])]})]}),makeQuery(id+"F38.opExtrude","SWEPT_FACE",FACE,{"disambiguationData":[OSD([subQ4,subQ3,subQ2,sQuery(id+"F20.wireOp",EDGE,"E11.top"),subQ0])]})]}),makeQuery(id+"F40.opExtrude","SWEPT_FACE",FACE,{"disambiguationData":[OSD([subQ4,subQ3,subQ2,subQ1,subQ0])]})]}),makeQuery(id+"F46.opExtrude","SWEPT_FACE",FACE,{"disambiguationData":[OSD([subQ4,subQ3,subQ2,subQ1,subQ0])]})]});}
            extrude(context, id + "F51", {"entities" : qUnion([Q0]), "operationType" : NewBodyOperationType.REMOVE, "endBound" : BoundingType.UP_TO_SURFACE, "oppositeDirection" : true, "endBoundEntityFace" : qUnion([Q1]), "depth" : 25.4 * mm});
        }
    });
